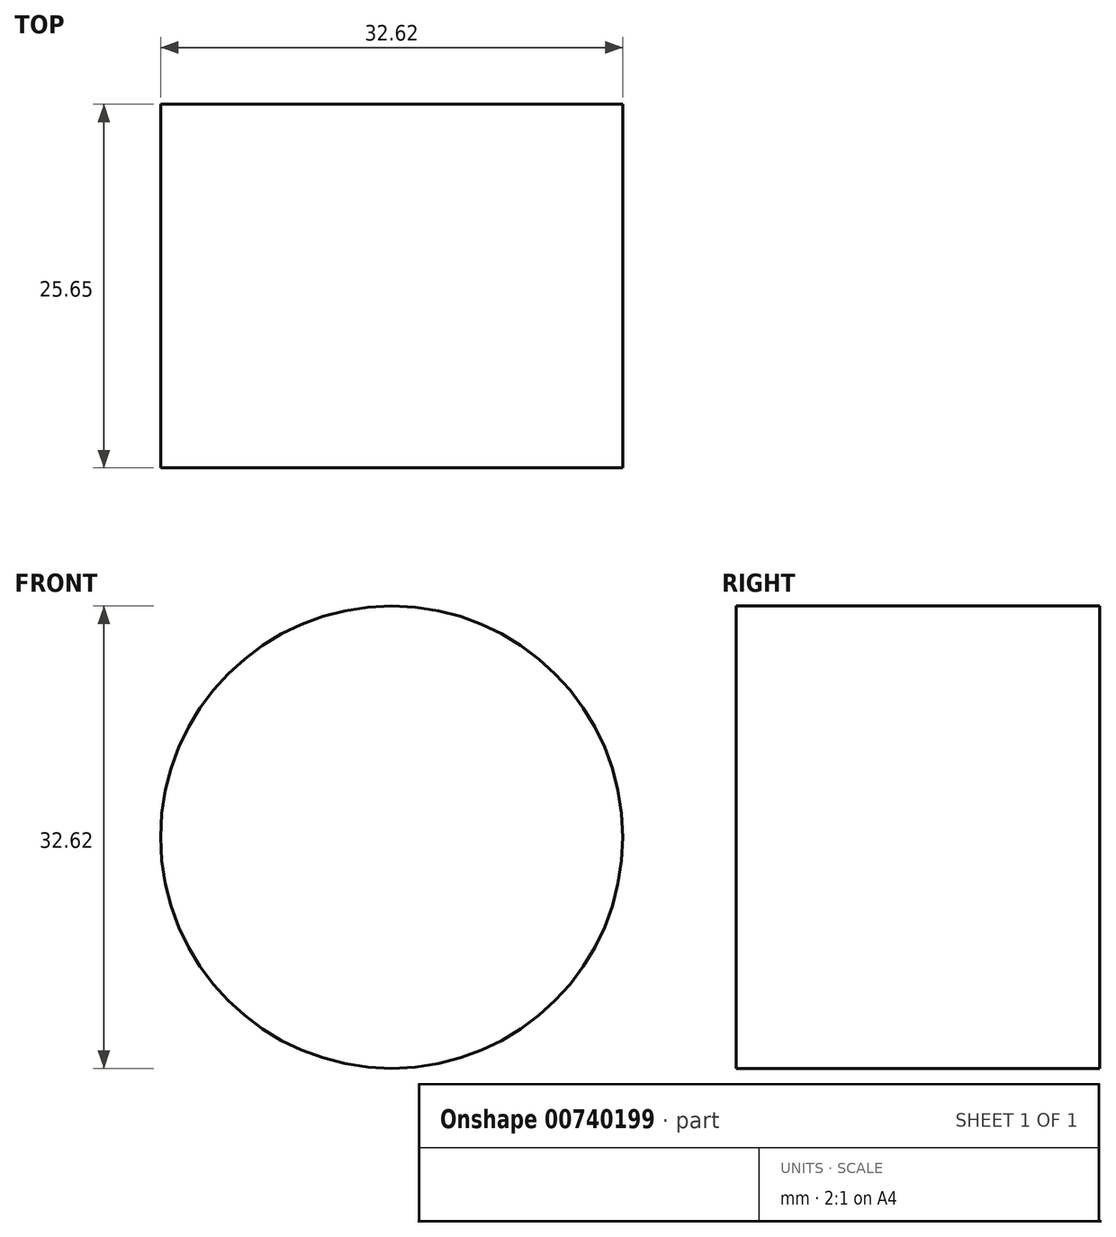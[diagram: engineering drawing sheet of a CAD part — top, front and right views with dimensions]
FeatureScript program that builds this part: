
annotation { "Feature Type Name" : "Feature", "Feature Type Description" : "" }
export const myFeature = defineFeature(function(context is Context, id is Id, definition is map)
    precondition{}
    {
        {
            var Q0;
            Q0=qCreatedBy(makeId("Front.planeOp"),FACE);
            var sketch = newSketch(context, id + "F0", { "sketchPlane" : qUnion([Q0])});
            skCircle(sketch, "E0", {"center": v(0, 0) * mm, "radius": 16.3 * mm});
            skSolve(sketch);
        }
        {
            var Q0;
            Q0 = qSketchRegion(id + "F0", true);
            extrude(context, id + "F1", {"entities" : qUnion([Q0]), "depth" : 25.65 * mm, "offsetDistance" : 25.4 * mm});
        }
    });
